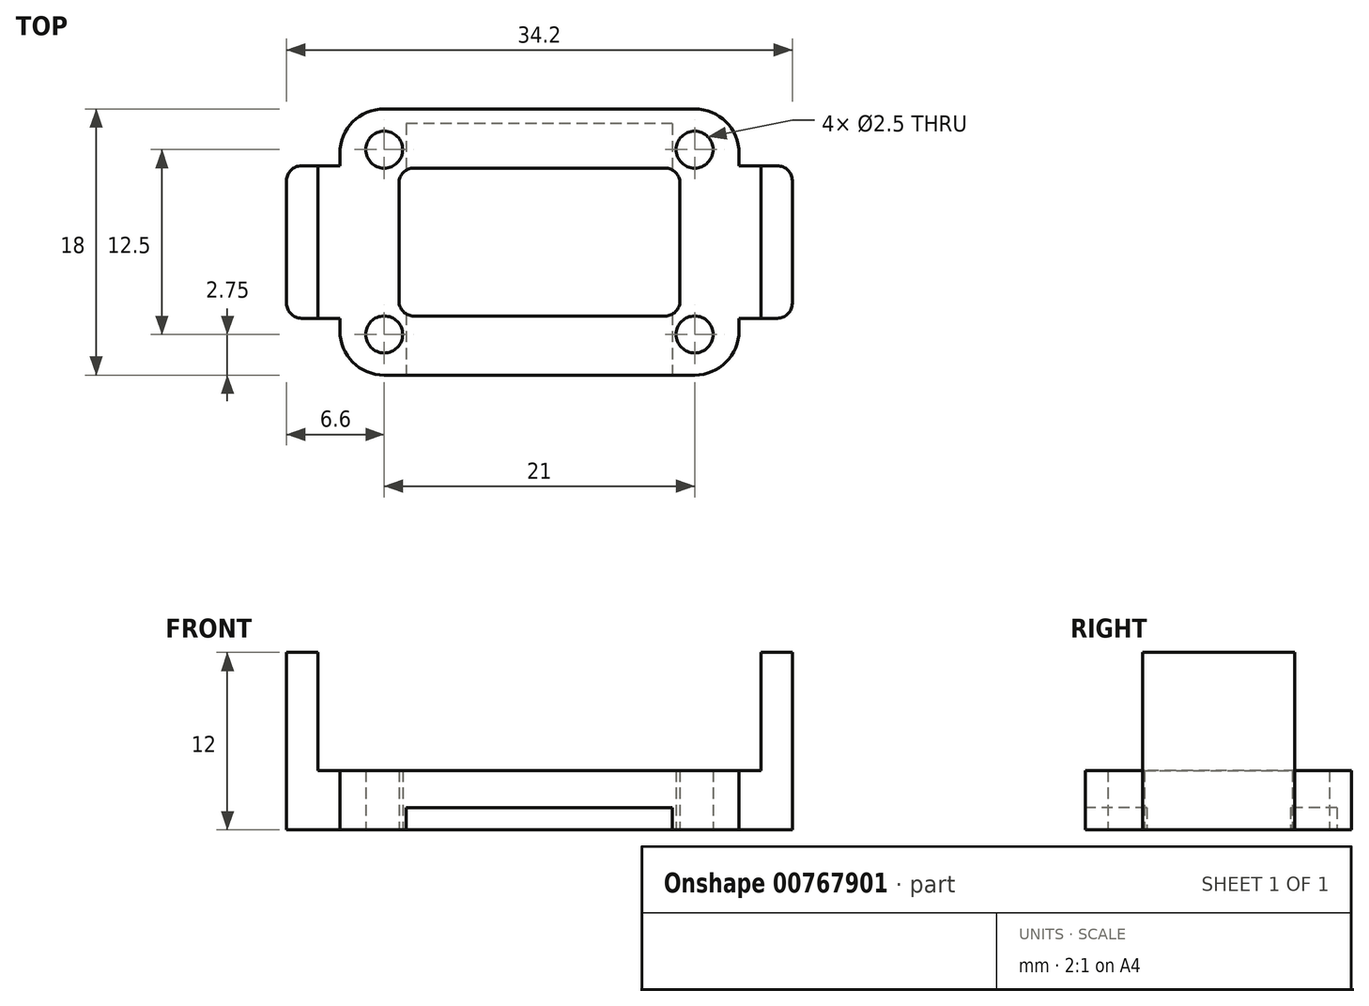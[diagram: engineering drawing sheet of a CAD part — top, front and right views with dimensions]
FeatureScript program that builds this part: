
annotation { "Feature Type Name" : "Feature", "Feature Type Description" : "" }
export const myFeature = defineFeature(function(context is Context, id is Id, definition is map)
    precondition{}
    {
        {
            var Q0;
            Q0=qCreatedBy(makeId("Top.planeOp"),FACE);
            var sketch = newSketch(context, id + "F0", { "sketchPlane" : qUnion([Q0])});
            skLineSegment(sketch, "E0.bottom", {"start": v(10.5, -9) * mm, "end": v(-10.5, -9) * mm});
            skLineSegment(sketch, "E0.top", {"start": v(10.5, 9) * mm, "end": v(-10.5, 9) * mm});
            skLineSegment(sketch, "E0.left", {"start": v(13.5, -6) * mm, "end": v(13.5, 6) * mm});
            skLineSegment(sketch, "E0.right", {"start": v(-13.5, -6) * mm, "end": v(-13.5, 6) * mm});
            skPoint(sketch, "E0.middle", {"position": v(0, 0) * mm});
            skLineSegment(sketch, "E1.bottom", {"start": v(8.5, -5) * mm, "end": v(-8.5, -5) * mm});
            skLineSegment(sketch, "E1.top", {"start": v(8.5, 5) * mm, "end": v(-8.5, 5) * mm});
            skLineSegment(sketch, "E1.left", {"start": v(9.5, -4) * mm, "end": v(9.5, 4) * mm});
            skLineSegment(sketch, "E1.right", {"start": v(-9.5, -4) * mm, "end": v(-9.5, 4) * mm});
            skPoint(sketch, "E2.visualSharp", {"position": v(-13.5, 9) * mm});
            skArc(sketch, "E2.filletArc", {"start": v(-10.5, 9) * mm, "mid": v(-12.62, 8.12) * mm, "end": v(-13.5, 6) * mm});
            skPoint(sketch, "E3.visualSharp", {"position": v(13.5, 9) * mm});
            skArc(sketch, "E3.filletArc", {"start": v(13.5, 6) * mm, "mid": v(12.62, 8.12) * mm, "end": v(10.5, 9) * mm});
            skPoint(sketch, "E4.visualSharp", {"position": v(13.5, -9) * mm});
            skArc(sketch, "E4.filletArc", {"start": v(10.5, -9) * mm, "mid": v(12.62, -8.12) * mm, "end": v(13.5, -6) * mm});
            skPoint(sketch, "E5.visualSharp", {"position": v(-13.5, -9) * mm});
            skArc(sketch, "E5.filletArc", {"start": v(-13.5, -6) * mm, "mid": v(-12.62, -8.12) * mm, "end": v(-10.5, -9) * mm});
            skPoint(sketch, "E6.visualSharp", {"position": v(-9.5, 5) * mm});
            skArc(sketch, "E6.filletArc", {"start": v(-8.5, 5) * mm, "mid": v(-9.2, 4.7) * mm, "end": v(-9.5, 4) * mm});
            skPoint(sketch, "E7.visualSharp", {"position": v(9.5, 5) * mm});
            skArc(sketch, "E7.filletArc", {"start": v(9.5, 4) * mm, "mid": v(9.2, 4.7) * mm, "end": v(8.5, 5) * mm});
            skPoint(sketch, "E8.visualSharp", {"position": v(9.5, -5) * mm});
            skArc(sketch, "E8.filletArc", {"start": v(8.5, -5) * mm, "mid": v(9.2, -4.7) * mm, "end": v(9.5, -4) * mm});
            skPoint(sketch, "E9.visualSharp", {"position": v(-9.5, -5) * mm});
            skArc(sketch, "E9.filletArc", {"start": v(-9.5, -4) * mm, "mid": v(-9.2, -4.7) * mm, "end": v(-8.5, -5) * mm});
            skLineSegment(sketch, "E10.bottom", {"start": v(-10.5, 6.25) * mm, "end": v(10.5, 6.25) * mm, "construction": true});
            skLineSegment(sketch, "E10.top", {"start": v(-10.5, -6.25) * mm, "end": v(10.5, -6.25) * mm, "construction": true});
            skLineSegment(sketch, "E10.left", {"start": v(-10.5, 6.25) * mm, "end": v(-10.5, -6.25) * mm, "construction": true});
            skLineSegment(sketch, "E10.right", {"start": v(10.5, 6.25) * mm, "end": v(10.5, -6.25) * mm, "construction": true});
            skCircle(sketch, "E11", {"center": v(-10.5, -6.25) * mm, "radius": 1.25 * mm});
            skCircle(sketch, "E12", {"center": v(10.5, -6.25) * mm, "radius": 1.25 * mm});
            skCircle(sketch, "E13", {"center": v(10.5, 6.25) * mm, "radius": 1.25 * mm});
            skCircle(sketch, "E14", {"center": v(-10.5, 6.25) * mm, "radius": 1.25 * mm});
            skLineSegment(sketch, "E15.bottom", {"start": v(16.1, 5.15) * mm, "end": v(13.5, 5.15) * mm});
            skLineSegment(sketch, "E15.top", {"start": v(16.1, -5.15) * mm, "end": v(13.5, -5.15) * mm});
            skLineSegment(sketch, "E15.left", {"start": v(17.1, 4.15) * mm, "end": v(17.1, -4.15) * mm});
            skLineSegment(sketch, "E15.right", {"start": v(13.5, 5.15) * mm, "end": v(13.5, -5.15) * mm});
            skPoint(sketch, "E16", {"position": v(13.5, 0) * mm});
            skLineSegment(sketch, "E17", {"start": v(0, 0) * mm, "end": v(0, 2.25) * mm, "construction": true});
            skLineSegment(sketch, "E18.MirrorCS", {"start": v(-16.1, -5.15) * mm, "end": v(-13.5, -5.15) * mm});
            skLineSegment(sketch, "E19.MirrorCS", {"start": v(-17.1, 4.15) * mm, "end": v(-17.1, -4.15) * mm});
            skLineSegment(sketch, "E20.MirrorCS", {"start": v(-16.1, 5.15) * mm, "end": v(-13.5, 5.15) * mm});
            skPoint(sketch, "E21.visualSharp", {"position": v(17.1, 5.15) * mm});
            skArc(sketch, "E21.filletArc", {"start": v(17.1, 4.15) * mm, "mid": v(16.8, 4.86) * mm, "end": v(16.1, 5.15) * mm});
            skPoint(sketch, "E22.visualSharp", {"position": v(17.1, -5.15) * mm});
            skArc(sketch, "E22.filletArc", {"start": v(16.1, -5.15) * mm, "mid": v(16.8, -4.86) * mm, "end": v(17.1, -4.15) * mm});
            skPoint(sketch, "E23.visualSharp", {"position": v(-17.1, 5.15) * mm});
            skArc(sketch, "E23.filletArc", {"start": v(-16.1, 5.15) * mm, "mid": v(-16.8, 4.86) * mm, "end": v(-17.1, 4.15) * mm});
            skPoint(sketch, "E24.visualSharp", {"position": v(-17.1, -5.15) * mm});
            skArc(sketch, "E24.filletArc", {"start": v(-17.1, -4.15) * mm, "mid": v(-16.8, -4.86) * mm, "end": v(-16.1, -5.15) * mm});
            skSolve(sketch);
        }
        {
            var Q0;
            Q0=makeQuery(id+"F0.imprint","IMPRINT",FACE,{"disambiguationData":[TD([[makeQuery(id+"F0.imprint","IMPRINT",EDGE,{"derivedFrom":sQuery(id+"F0.wireOp",EDGE,"E0.bottom")}),-1.0]])]});
            var Q1;
            Q1=makeQuery(id+"F0.imprint","IMPRINT",FACE,{"disambiguationData":[TD([[makeQuery(id+"F0.imprint","IMPRINT",EDGE,{"derivedFrom":sQuery(id+"F0.wireOp",EDGE,"E15.bottom")}),1.0]])]});
            var Q2;
            {var subQ0=sQuery(id+"F0.wireOp",EDGE,"E18.MirrorCS");Q2=makeQuery(id+"F0.imprint","IMPRINT",FACE,{"disambiguationData":[TD([[makeQuery(id+"F0.imprint","IMPRINT",EDGE,{"derivedFrom":subQ0}),1.0]])]});}
            extrude(context, id + "F1", {"entities" : qUnion([Q0, Q1, Q2]), "depth" : 4 * mm, "offsetDistance" : 25 * mm});
        }
        {
            var Q0;
            Q0=makeQuery(id+"F1.opExtrude","CAP_FACE",FACE,{"disambiguationData":[OSD([sQuery(id+"F0.wireOp",EDGE,"E0.bottom"),sQuery(id+"F0.wireOp",EDGE,"E0.top"),sQuery(id+"F0.wireOp",EDGE,"E0.left"),sQuery(id+"F0.wireOp",EDGE,"E0.right"),sQuery(id+"F0.wireOp",EDGE,"E1.bottom"),sQuery(id+"F0.wireOp",EDGE,"E1.top"),sQuery(id+"F0.wireOp",EDGE,"E1.left"),sQuery(id+"F0.wireOp",EDGE,"E1.right"),sQuery(id+"F0.wireOp",EDGE,"E2.filletArc"),sQuery(id+"F0.wireOp",EDGE,"E3.filletArc"),sQuery(id+"F0.wireOp",EDGE,"E4.filletArc"),sQuery(id+"F0.wireOp",EDGE,"E5.filletArc"),sQuery(id+"F0.wireOp",EDGE,"E6.filletArc"),sQuery(id+"F0.wireOp",EDGE,"E7.filletArc"),sQuery(id+"F0.wireOp",EDGE,"E8.filletArc"),sQuery(id+"F0.wireOp",EDGE,"E9.filletArc"),sQuery(id+"F0.wireOp",EDGE,"E11"),sQuery(id+"F0.wireOp",EDGE,"E12"),sQuery(id+"F0.wireOp",EDGE,"E13"),sQuery(id+"F0.wireOp",EDGE,"E14")])],"isStart":true});
            var sketch = newSketch(context, id + "F2", { "sketchPlane" : qUnion([Q0])});
            skLineSegment(sketch, "E25.bottom", {"start": v(9, -8) * mm, "end": v(-9, -8) * mm});
            skLineSegment(sketch, "E25.top", {"start": v(9, 9) * mm, "end": v(-9, 9) * mm});
            skLineSegment(sketch, "E25.left", {"start": v(9, -8) * mm, "end": v(9, 9) * mm});
            skLineSegment(sketch, "E25.right", {"start": v(-9, -8) * mm, "end": v(-9, 9) * mm});
            skLineSegment(sketch, "E26", {"start": v(0, 9) * mm, "end": v(0, -8) * mm, "construction": true});
            skSolve(sketch);
        }
        {
            var Q0;
            Q0 = qSketchRegion(id + "F2", true);
            extrude(context, id + "F3", {"entities" : qUnion([Q0]), "operationType" : NewBodyOperationType.REMOVE, "oppositeDirection" : true, "depth" : 1.5 * mm, "offsetDistance" : 25 * mm});
        }
        {
            var Q0;
            Q0=makeQuery(id+"F1.opExtrude","CAP_FACE",FACE,{"disambiguationData":[OSD([sQuery(id+"F0.wireOp",EDGE,"E0.bottom"),sQuery(id+"F0.wireOp",EDGE,"E0.top"),sQuery(id+"F0.wireOp",EDGE,"E0.left"),sQuery(id+"F0.wireOp",EDGE,"E0.right"),sQuery(id+"F0.wireOp",EDGE,"E1.bottom"),sQuery(id+"F0.wireOp",EDGE,"E1.top"),sQuery(id+"F0.wireOp",EDGE,"E1.left"),sQuery(id+"F0.wireOp",EDGE,"E1.right"),sQuery(id+"F0.wireOp",EDGE,"E2.filletArc"),sQuery(id+"F0.wireOp",EDGE,"E3.filletArc"),sQuery(id+"F0.wireOp",EDGE,"E4.filletArc"),sQuery(id+"F0.wireOp",EDGE,"E5.filletArc"),sQuery(id+"F0.wireOp",EDGE,"E6.filletArc"),sQuery(id+"F0.wireOp",EDGE,"E7.filletArc"),sQuery(id+"F0.wireOp",EDGE,"E8.filletArc"),sQuery(id+"F0.wireOp",EDGE,"E9.filletArc"),sQuery(id+"F0.wireOp",EDGE,"E11"),sQuery(id+"F0.wireOp",EDGE,"E12"),sQuery(id+"F0.wireOp",EDGE,"E13"),sQuery(id+"F0.wireOp",EDGE,"E14"),sQuery(id+"F0.wireOp",EDGE,"E15.bottom"),sQuery(id+"F0.wireOp",EDGE,"E15.top"),sQuery(id+"F0.wireOp",EDGE,"E15.left"),sQuery(id+"F0.wireOp",EDGE,"E18.MirrorCS"),sQuery(id+"F0.wireOp",EDGE,"E19.MirrorCS"),sQuery(id+"F0.wireOp",EDGE,"E20.MirrorCS"),sQuery(id+"F0.wireOp",EDGE,"E21.filletArc"),sQuery(id+"F0.wireOp",EDGE,"E22.filletArc"),sQuery(id+"F0.wireOp",EDGE,"E23.filletArc"),sQuery(id+"F0.wireOp",EDGE,"E24.filletArc")])],"isStart":false});
            var sketch = newSketch(context, id + "F4", { "sketchPlane" : qUnion([Q0])});
            skLineSegment(sketch, "E27.0", {"start": v(-17.1, 4.15) * mm, "end": v(-17.1, -4.15) * mm});
            skArc(sketch, "E28.0", {"start": v(-16.1, 5.15) * mm, "mid": v(-16.8, 4.86) * mm, "end": v(-17.1, 4.15) * mm});
            skArc(sketch, "E29.0", {"start": v(-17.1, -4.15) * mm, "mid": v(-16.8, -4.86) * mm, "end": v(-16.1, -5.15) * mm});
            skLineSegment(sketch, "E30.0", {"start": v(-16.1, -5.15) * mm, "end": v(-13.5, -5.15) * mm});
            skLineSegment(sketch, "E31.0", {"start": v(-16.1, 5.15) * mm, "end": v(-13.5, 5.15) * mm});
            skLineSegment(sketch, "E32", {"start": v(-15, 5.15) * mm, "end": v(-13.5, 5.15) * mm});
            skLineSegment(sketch, "E33", {"start": v(-15, 5.15) * mm, "end": v(-15, -5.15) * mm});
            skLineSegment(sketch, "E34", {"start": v(-13.5, -5.15) * mm, "end": v(-15, -5.15) * mm});
            skLineSegment(sketch, "E35", {"start": v(0, 0.46) * mm, "end": v(0, 2.38) * mm, "construction": true});
            skLineSegment(sketch, "E36.MirrorCS", {"start": v(13.5, -5.15) * mm, "end": v(15, -5.15) * mm});
            skLineSegment(sketch, "E37.MirrorCS", {"start": v(16.1, 5.15) * mm, "end": v(13.5, 5.15) * mm});
            skLineSegment(sketch, "E38.MirrorCS", {"start": v(15, 5.15) * mm, "end": v(13.5, 5.15) * mm});
            skLineSegment(sketch, "E39.MirrorCS", {"start": v(16.1, -5.15) * mm, "end": v(13.5, -5.15) * mm});
            skArc(sketch, "E40.MirrorCS", {"start": v(17.1, -4.15) * mm, "mid": v(16.8, -4.86) * mm, "end": v(16.1, -5.15) * mm});
            skLineSegment(sketch, "E41.MirrorCS", {"start": v(17.1, 4.15) * mm, "end": v(17.1, -4.15) * mm});
            skLineSegment(sketch, "E42.MirrorCS", {"start": v(15, 5.15) * mm, "end": v(15, -5.15) * mm});
            skArc(sketch, "E43.MirrorCS", {"start": v(16.1, 5.15) * mm, "mid": v(16.8, 4.86) * mm, "end": v(17.1, 4.15) * mm});
            skSolve(sketch);
        }
        {
            var Q0;
            Q0 = qSketchRegion(id + "F4", true);
            extrude(context, id + "F5", {"entities" : qUnion([Q0]), "operationType" : NewBodyOperationType.ADD, "depth" : 8 * mm, "offsetDistance" : 25 * mm});
        }
    });
